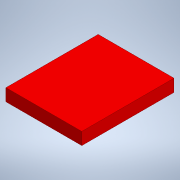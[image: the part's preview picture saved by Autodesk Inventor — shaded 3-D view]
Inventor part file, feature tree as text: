
AUTODESK INVENTOR PART (.ipt)
format: ipt  version: 2020 (Build 240168000, 168)  size: 95,744 bytes
history: native  units: mm
features: extrude x1, sketch x1
ambient origin geometry x8: Origin, YZ Plane, XZ Plane, XY Plane, X Axis, Y Axis, Z Axis, Center Point
bodies: Solid1 (feature_tree)
feature tree (2):
  extrude  "Extrusion1"  Depth=22.5mm
  sketch  "Sketch1"  dims[d0=18.5mm d1=22.5mm d2=3.0mm d3=0.0mm]
